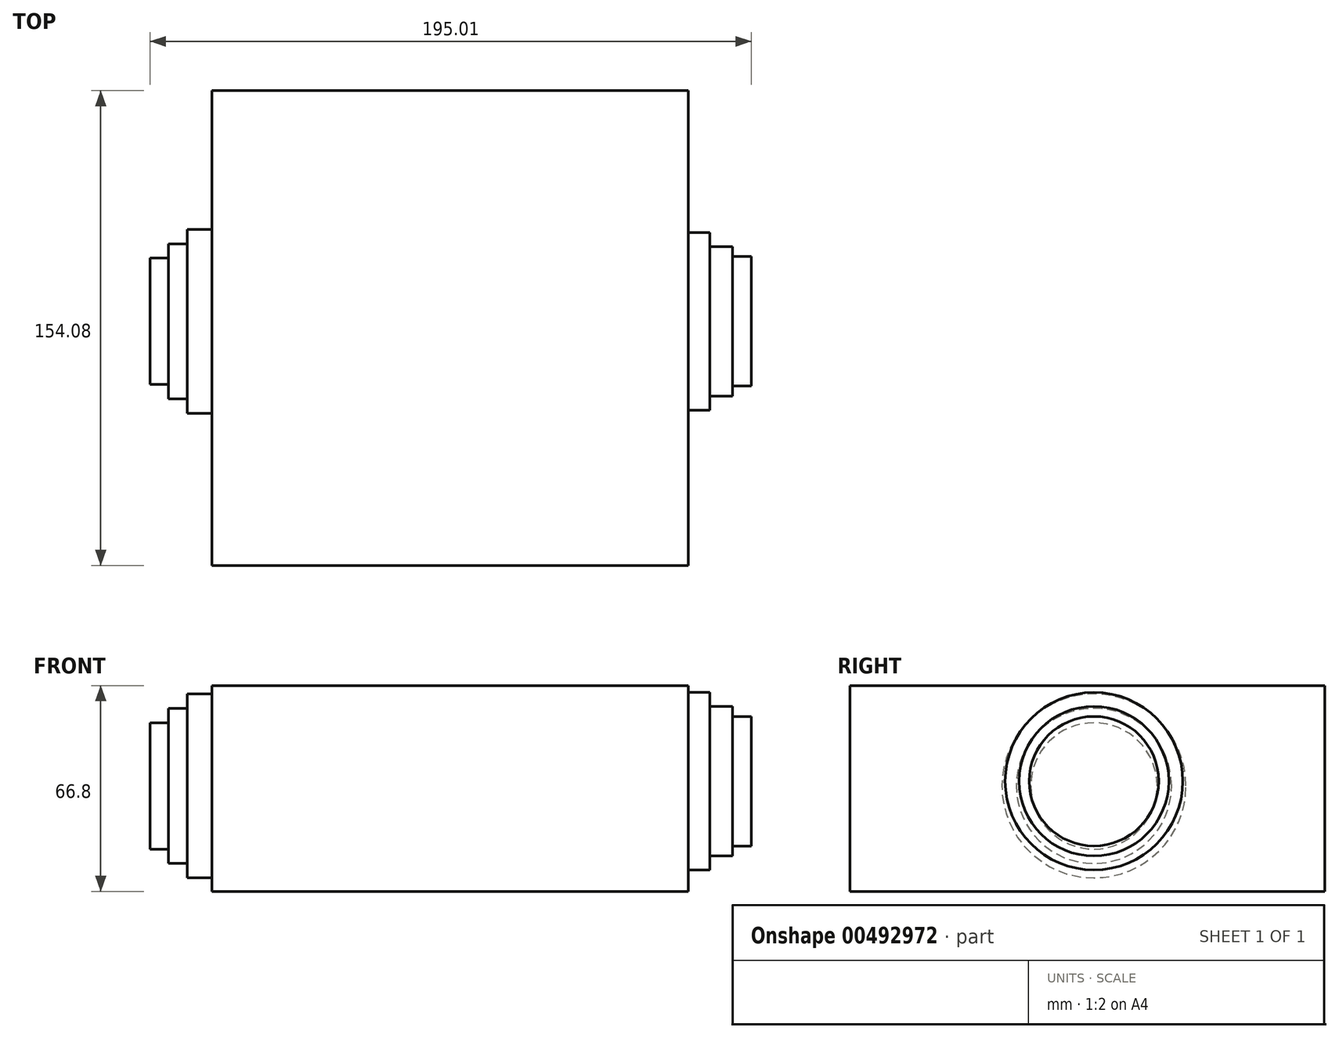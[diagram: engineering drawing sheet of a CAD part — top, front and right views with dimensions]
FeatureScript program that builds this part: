
annotation { "Feature Type Name" : "Feature", "Feature Type Description" : "" }
export const myFeature = defineFeature(function(context is Context, id is Id, definition is map)
    precondition{}
    {
        {
            var Q0;
            Q0=qCreatedBy(makeId("Top.planeOp"),FACE);
            var sketch = newSketch(context, id + "F0", { "sketchPlane" : qUnion([Q0])});
            skLineSegment(sketch, "E0.bottom", {"start": v(-74.85, 74.87) * mm, "end": v(79.76, 74.87) * mm});
            skLineSegment(sketch, "E0.top", {"start": v(-74.85, -79.2) * mm, "end": v(79.76, -79.2) * mm});
            skLineSegment(sketch, "E0.left", {"start": v(-74.85, 74.87) * mm, "end": v(-74.85, -79.2) * mm});
            skLineSegment(sketch, "E0.right", {"start": v(79.76, 74.87) * mm, "end": v(79.76, -79.2) * mm});
            skSolve(sketch);
        }
        {
            var Q0;
            Q0=makeQuery(id+"F0.imprint","IMPRINT",FACE,{"disambiguationData":[TD([[makeQuery(id+"F0.imprint","IMPRINT",EDGE,{"derivedFrom":sQuery(id+"F0.wireOp",EDGE,"E0.bottom")}),-1.0]])]});
            extrude(context, id + "F1", {"entities" : qUnion([Q0]), "depth" : 66.8 * mm});
        }
        {
            var Q0;
            Q0=makeQuery(id+"F1.opExtrude","SWEPT_FACE",FACE,{"disambiguationData":[OSD([sQuery(id+"F0.wireOp",EDGE,"E0.right")])]});
            var sketch = newSketch(context, id + "F2", { "sketchPlane" : qUnion([Q0])});
            skCircle(sketch, "E1", {"center": v(0, 35.76) * mm, "radius": 28.81 * mm});
            skSolve(sketch);
        }
        {
            var Q0;
            Q0=makeQuery(id+"F2.imprint","IMPRINT",FACE,{"disambiguationData":[TD([[makeQuery(id+"F2.imprint","IMPRINT",EDGE,{"derivedFrom":sQuery(id+"F2.wireOp",EDGE,"E1")}),1.0]])]});
            extrude(context, id + "F3", {"entities" : qUnion([Q0]), "operationType" : NewBodyOperationType.ADD, "depth" : 7 * mm});
        }
        {
            var Q0;
            Q0=makeQuery(id+"F3.opExtrude","CAP_FACE",FACE,{"disambiguationData":[OSD([sQuery(id+"F2.wireOp",EDGE,"E1")])],"isStart":false});
            var sketch = newSketch(context, id + "F4", { "sketchPlane" : qUnion([Q0])});
            skCircle(sketch, "E2", {"center": v(0, 35.76) * mm, "radius": 24.29 * mm});
            skSolve(sketch);
        }
        {
            var Q0;
            Q0 = qSketchRegion(id + "F4", true);
            extrude(context, id + "F5", {"entities" : qUnion([Q0]), "operationType" : NewBodyOperationType.ADD, "depth" : 7.3 * mm});
        }
        {
            var Q0;
            Q0=makeQuery(id+"F5.opExtrude","CAP_FACE",FACE,{"disambiguationData":[OSD([sQuery(id+"F4.wireOp",EDGE,"E2")])],"isStart":false});
            var sketch = newSketch(context, id + "F6", { "sketchPlane" : qUnion([Q0])});
            skCircle(sketch, "E3", {"center": v(0, 35.76) * mm, "radius": 21.01 * mm});
            skSolve(sketch);
        }
        {
            var Q0;
            Q0=makeQuery(id+"F6.imprint","IMPRINT",FACE,{"disambiguationData":[TD([[makeQuery(id+"F6.imprint","IMPRINT",EDGE,{"derivedFrom":sQuery(id+"F6.wireOp",EDGE,"E3")}),1.0]])]});
            extrude(context, id + "F7", {"entities" : qUnion([Q0]), "operationType" : NewBodyOperationType.ADD, "depth" : 6.1 * mm});
        }
        {
            var Q0;
            Q0=makeQuery(id+"F1.opExtrude","SWEPT_FACE",FACE,{"disambiguationData":[OSD([sQuery(id+"F0.wireOp",EDGE,"E0.left")])]});
            var sketch = newSketch(context, id + "F8", { "sketchPlane" : qUnion([Q0])});
            skCircle(sketch, "E4", {"center": v(0, 34.22) * mm, "radius": 29.85 * mm});
            skSolve(sketch);
        }
        {
            var Q0;
            Q0=makeQuery(id+"F8.imprint","IMPRINT",FACE,{"disambiguationData":[TD([[makeQuery(id+"F8.imprint","IMPRINT",EDGE,{"derivedFrom":sQuery(id+"F8.wireOp",EDGE,"E4")}),1.0]])]});
            extrude(context, id + "F9", {"entities" : qUnion([Q0]), "operationType" : NewBodyOperationType.ADD, "depth" : 8 * mm});
        }
        {
            var Q0;
            Q0=makeQuery(id+"F9.opExtrude","CAP_FACE",FACE,{"disambiguationData":[OSD([sQuery(id+"F8.wireOp",EDGE,"E4")])],"isStart":false});
            var sketch = newSketch(context, id + "F10", { "sketchPlane" : qUnion([Q0])});
            skCircle(sketch, "E5", {"center": v(0, 34.22) * mm, "radius": 25.17 * mm});
            skSolve(sketch);
        }
        {
            var Q0;
            Q0=makeQuery(id+"F10.imprint","IMPRINT",FACE,{"disambiguationData":[TD([[makeQuery(id+"F10.imprint","IMPRINT",EDGE,{"derivedFrom":sQuery(id+"F10.wireOp",EDGE,"E5")}),1.0]])]});
            extrude(context, id + "F11", {"entities" : qUnion([Q0]), "operationType" : NewBodyOperationType.ADD, "depth" : 6 * mm});
        }
        {
            var Q0;
            Q0=makeQuery(id+"F11.opExtrude","CAP_FACE",FACE,{"disambiguationData":[OSD([sQuery(id+"F10.wireOp",EDGE,"E5")])],"isStart":false});
            var sketch = newSketch(context, id + "F12", { "sketchPlane" : qUnion([Q0])});
            skCircle(sketch, "E6", {"center": v(0, 34.22) * mm, "radius": 20.5 * mm});
            skSolve(sketch);
        }
        {
            var Q0;
            Q0=makeQuery(id+"F12.imprint","IMPRINT",FACE,{"disambiguationData":[TD([[makeQuery(id+"F12.imprint","IMPRINT",EDGE,{"derivedFrom":sQuery(id+"F12.wireOp",EDGE,"E6")}),1.0]])]});
            extrude(context, id + "F13", {"entities" : qUnion([Q0]), "operationType" : NewBodyOperationType.ADD, "depth" : 6 * mm});
        }
    });
